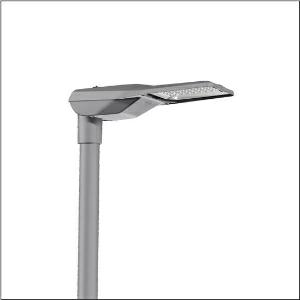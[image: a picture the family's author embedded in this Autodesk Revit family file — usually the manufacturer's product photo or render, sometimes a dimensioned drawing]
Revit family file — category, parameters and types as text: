
# Revit family: streetlight_sl_21_iq_mini___st1_0a_5xe2d31v08hb_a16f
name_source: partatom
category: Lighting Fixtures
units: mm (PartAtom-declared; Revit-internal decimal feet)

## family parameters
Cut with Voids When Loaded = No
Host = Face
Light Source = No
Part Type = Normal
Room Calculation Point = No
Round Connector Dimension = Use Diameter
Shared = No

## types (1)
- --- (1 x LED, 9750 lm, 71 W, 3000K)
    Apparent Load = 71 VA
    CIE Flux Codes = 37 72 97 100 100
    Color Rendering = 70
    Color Temperature = 3000K
    Default Elevation = 1800 mm
    Description = Streetlight SL 21 iQ mini, mast luminaire, primary light control with lens, of PMMA, primary optical cover: cover, of toughened safety glass, transparent, light distribution: ST1.0a, light emission: direct distribution, primary light characteristic: asymmetric, installation type: post-top, side-entry, LED, High Power LED, rated luminous flux: 9.750lm, luminous efficacy: 137lm/W, light colour: 730, colour temperature: 3000K, control: presetting dimming logarithmic, Street-Remote, Auto-Match, Temp-Guard, Lumen-Switch, Night-Set, Smart-Wire, Light-Fading, Desk-Remote (wireless, voltage-free reading and setting of iQ features in the workshop via application-optimized NFC function/RFID function), optimised constant luminous flux control (CLO 2.0), mains connection: 220..240V, AC, 50/60Hz, start of lifetime: 71W, end of service life: 75W, reduction: 30W, luminaire housing, of diecast aluminium, powder-coated, Siteco® metallic grey (DB 702S), corrosivity category C5 mid according to DIN EN ISO 12944, please order mast flange separately, inclination adjustable: 0°, 5°, 10°, 15°, sealing non-destructively replaceable, multi-level sealing system, length: 628mm, width: 235mm, height: 110mm, mast flange for spigot size: 42mm (side-entry): 5XC10008XM4, 60/48mm (side-entry/post-top): 5XC10108XM2, 76/60mm (side-entry/post-top): 5XC10108XM1, Smart Interface above, protection rating (complete): IP66, insulation class (complete): insulation class II (safety insulation), certification: CE, ENEC, ENEC+, VDE, impact resistance: IK09, permissible operating ambient temperature for outdoor applications: -40..+50°C, standard-compliant lighting for roads and squares, packaging unit: 1 piece

Light Distribution: ST1.0a
    Height = 110 mm
    Lamp = 1 x LED
    Lamp Light Flux = 9750 lm
    Lamp Power = 71 W
    Lamp count = 1
    Length = 625 mm
    Luminous efficacy = 137 lm/W
    Manufacturer = Siteco
    ModVariant = No
    Model = 5XE2D31V08HB
    Number of Poles = 1
    OnlyDefault = Yes
    Power Factor = 1
    Product Name = Streetlight SL 21 iQ mini | ST1.0a
    Product group = mast luminaire | pylon top
    ProductGroupID = 6100
    Protection Class = Protection class II
    Protection Degree = IP 66
    RLX_Detail_Level = 1
    RLX_Emergency_Light_Flux = 0 lm
    RLX_Emergency_Type = 0
    RLX_Emergency_Type_DB = No
    RlxData = <blob elided: 92437 chars, md5=98727e43>
    Socket = socket
    Standby Power = 0 W
    System Light Flux = 9750 lm
    System Power = 71 W
    Type Comments = factory setting: luminous flux: 100 % | dim-lin: 254 | 716 mA
    Type Image = l_1003515.jpg
    URL = http://relux.com
    VarID = @adj_063307
    Voltage = 0 V
    Weight = 0.00 kg
    Width = 234 mm

## geometry (parser evidence)
native form markers: Blend x4, Sweep x11
no freeform markers — native parametric forms only
